# Revit family: Water_Heater-Navien-Condensing-NPE-A2
name_source: partatom
category: Mechanical Equipment
units: mm (PartAtom-declared; Revit-internal decimal feet)

## family parameters
Cut with Voids When Loaded = No
Host = Face
OmniClass Number = 23.65.35.11
OmniClass Title = Supply Water Heaters
Part Type = Normal
Room Calculation Point = No
Round Connector Dimension = Use Diameter
Shared = No

## types (3) — shared parameters
2" Exhaust/Intake = Yes
3" Exhaust/Intake = No
Apparent Load = 0 VA
Assembly Code = D3010500
Certifications = Energy Star | AHRI | CSA | ASME | CSA Blue Star | CSA Blue Flame
Cold Water Inlet = 0.75 "
Default Elevation = 48 "
Depth = 13.2 "
Description = NPE-A2 Advanced Condensing Tankless Gas Water Heaters
Exhaust = 2"
Finish = Metal - Navien - White
Frequency = 60 Hz
Gas Inlet = 1"
Height = 28.8 "
Hot Water Inlet = 0.75 "
Ignition = Electronic ignition
Installation Type = Outdoor Wall-Hung Only
Intake = 2"
Keynote = 22 33 00.A1
Manufacturer = Navien, Inc.
Manufacturer Fax Number = (949) 420-0430
Natural Gas Supply Pressure = 3.5" to 10.5" WC
Number of Poles = 1
Phase = 1
Power Factor = 1
Product Documentation Link = https://www.navieninc.com
Product Name = NPE-A2 Advanced Series Tankless Water Heaters
Product Page URL = https://www.navieninc.com
Propane Gas Supply Pressure = 8.0" to 13" WC
URL = https://www.navieninc.com
Venting = No Venting (Outdoor Installation Only)
Venting Type = 2" or 3" PVC, CPVC, approved polypropylene and stainless steel
Version = 2019 - v1.0.a
Voltage = 120 V
Warranty = https://www.navieninc.com
Warranty Note = Heat Exchangers: 15 years limited warranty (Residential) | Parts: 5 years (Residential)
Water Pressure = 15-150 psi
Wi-Fi Ready = NaviLink Wi‑Fi Control: This add-on accessory enables access to control temperatures remotely, access usage data and receive diagnostic notifications via smartphone or tablet.
Width = 17.3 "

## per-type parameters (varying)
| type | Constraints | Heating Capacity | Heating Capacity Note | Natural Gas Manifold Pressure | Propane Gas Manifold Pressure | Weight |
| NPE-180A2 | 1 | 150000.0 Btu/h | 10,000 to 150,000 BTUh | 0.03" to 0.55" WC | 0.03" to 0.55" WC | 73.00 lbf |
| NPE-210A2 | 2 | 180000.0 Btu/h | 12,000 to 180,000 BTUh | 0.03" to 0.76" WC | 0.02" to 0.76" WC | 77.00 lbf |
| NPE-240A2 | 3 | 199900.0 Btu/h | 13,300 to 199,990 BTUh | 0.03" to 0.96" WC | 0.02" to 0.96" WC | 77.00 lbf |

note: column(s) folded — value = type name in every type: Model

## geometry (parser evidence)
native form markers: Blend x4, Sweep x6
no freeform markers — native parametric forms only
